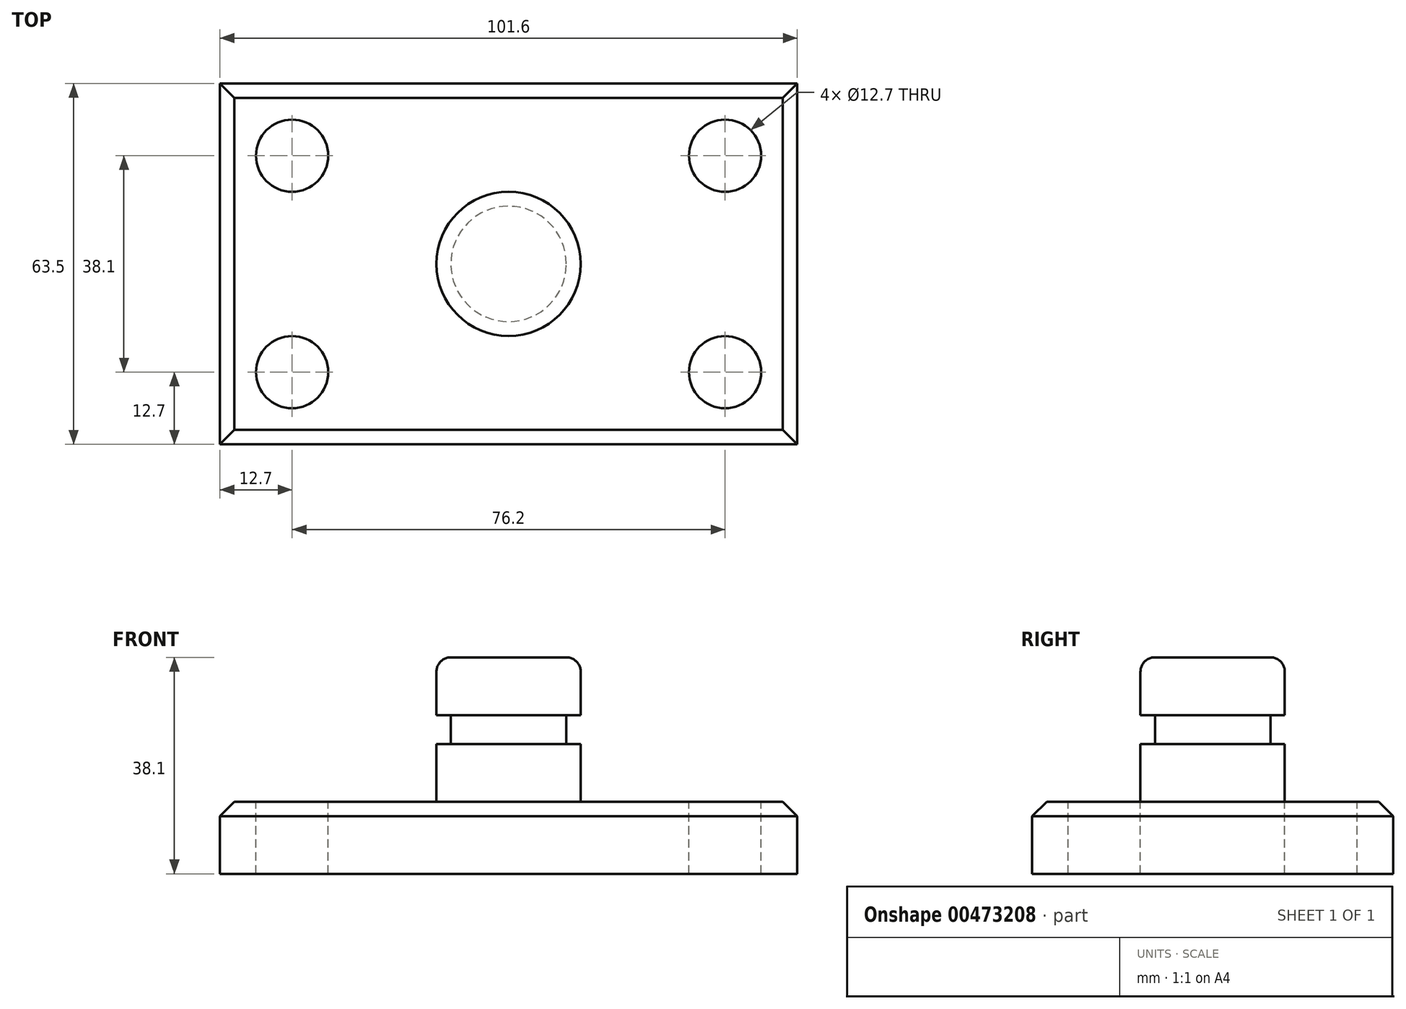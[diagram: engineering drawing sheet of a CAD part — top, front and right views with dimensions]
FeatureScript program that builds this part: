
annotation { "Feature Type Name" : "Feature", "Feature Type Description" : "" }
export const myFeature = defineFeature(function(context is Context, id is Id, definition is map)
    precondition{}
    {
        {
            var Q0;
            Q0=qCreatedBy(makeId("Top.planeOp"),FACE);
            var sketch = newSketch(context, id + "F0", { "sketchPlane" : qUnion([Q0])});
            skLineSegment(sketch, "E0.bottom", {"start": v(50.8, 31.75) * mm, "end": v(-50.8, 31.75) * mm});
            skLineSegment(sketch, "E0.top", {"start": v(50.8, -31.75) * mm, "end": v(-50.8, -31.75) * mm});
            skLineSegment(sketch, "E0.left", {"start": v(50.8, 31.75) * mm, "end": v(50.8, -31.75) * mm});
            skLineSegment(sketch, "E0.right", {"start": v(-50.8, 31.75) * mm, "end": v(-50.8, -31.75) * mm});
            skPoint(sketch, "E0.middle", {"position": v(0, 0) * mm});
            skSolve(sketch);
        }
        {
            var Q0;
            Q0=makeQuery(id+"F0.imprint","IMPRINT",FACE,{"disambiguationData":[TD([[makeQuery(id+"F0.imprint","IMPRINT",EDGE,{"derivedFrom":sQuery(id+"F0.wireOp",EDGE,"E0.bottom")}),1.0]])]});
            extrude(context, id + "F1", {"entities" : qUnion([Q0]), "depth" : 12.7 * mm});
        }
        {
            var Q0;
            Q0=makeQuery(id+"F1.opExtrude","CAP_FACE",FACE,{"disambiguationData":[OSD([sQuery(id+"F0.wireOp",EDGE,"E0.bottom"),sQuery(id+"F0.wireOp",EDGE,"E0.top"),sQuery(id+"F0.wireOp",EDGE,"E0.left"),sQuery(id+"F0.wireOp",EDGE,"E0.right")])],"isStart":false});
            var sketch = newSketch(context, id + "F2", { "sketchPlane" : qUnion([Q0])});
            skCircle(sketch, "E1", {"center": v(-38.1, 19.05) * mm, "radius": 6.35 * mm});
            skCircle(sketch, "E2", {"center": v(38.1, 19.05) * mm, "radius": 6.35 * mm});
            skCircle(sketch, "E3", {"center": v(38.1, -19.05) * mm, "radius": 6.35 * mm});
            skCircle(sketch, "E4", {"center": v(-38.1, -19.05) * mm, "radius": 6.35 * mm});
            skSolve(sketch);
        }
        {
            var Q0;
            Q0=makeQuery(id+"F2.imprint","IMPRINT",FACE,{"disambiguationData":[TD([[makeQuery(id+"F2.imprint","IMPRINT",EDGE,{"derivedFrom":sQuery(id+"F2.wireOp",EDGE,"E1")}),1.0]])]});
            var Q1;
            Q1=makeQuery(id+"F2.imprint","IMPRINT",FACE,{"disambiguationData":[TD([[makeQuery(id+"F2.imprint","IMPRINT",EDGE,{"derivedFrom":sQuery(id+"F2.wireOp",EDGE,"E4")}),1.0]])]});
            var Q2;
            Q2=makeQuery(id+"F2.imprint","IMPRINT",FACE,{"disambiguationData":[TD([[makeQuery(id+"F2.imprint","IMPRINT",EDGE,{"derivedFrom":sQuery(id+"F2.wireOp",EDGE,"E3")}),1.0]])]});
            var Q3;
            Q3=makeQuery(id+"F2.imprint","IMPRINT",FACE,{"disambiguationData":[TD([[makeQuery(id+"F2.imprint","IMPRINT",EDGE,{"derivedFrom":sQuery(id+"F2.wireOp",EDGE,"E2")}),1.0]])]});
            extrude(context, id + "F3", {"entities" : qUnion([Q0, Q1, Q2, Q3]), "operationType" : NewBodyOperationType.REMOVE, "endBound" : BoundingType.THROUGH_ALL, "oppositeDirection" : true, "depth" : 25.4 * mm});
        }
        {
            var Q0;
            Q0=qCreatedBy(makeId("Front.planeOp"),FACE);
            var sketch = newSketch(context, id + "F4", { "sketchPlane" : qUnion([Q0])});
            skLineSegment(sketch, "E5.bottom", {"start": v(0, 12.7) * mm, "end": v(12.7, 12.7) * mm});
            skLineSegment(sketch, "E5.top", {"start": v(0, 38.1) * mm, "end": v(12.7, 38.1) * mm});
            skLineSegment(sketch, "E5.left", {"start": v(0, 12.7) * mm, "end": v(0, 38.1) * mm});
            skLineSegment(sketch, "E5.right", {"start": v(12.7, 12.7) * mm, "end": v(12.7, 38.1) * mm});
            skSolve(sketch);
        }
        {
            var Q0;
            Q0=makeQuery(id+"F4.imprint","IMPRINT",FACE,{"disambiguationData":[TD([[makeQuery(id+"F4.imprint","IMPRINT",EDGE,{"derivedFrom":sQuery(id+"F4.wireOp",EDGE,"E5.bottom")}),1.0]])]});
            var Q1;
            Q1=sQuery(id+"F4.wireOp",EDGE,"E5.left");
            revolve(context, id + "F5", {"operationType" : NewBodyOperationType.ADD, "entities" : qUnion([Q0]), "axis" : qUnion([Q1]), "revolveType" : RevolveType.FULL});
        }
        {
            var Q0;
            Q0=qCreatedBy(makeId("Front.planeOp"),FACE);
            var sketch = newSketch(context, id + "F6", { "sketchPlane" : qUnion([Q0])});
            skLineSegment(sketch, "E6.bottom", {"start": v(14.97, 27.94) * mm, "end": v(10.16, 27.94) * mm});
            skLineSegment(sketch, "E6.top", {"start": v(14.97, 22.86) * mm, "end": v(10.16, 22.86) * mm});
            skLineSegment(sketch, "E6.left", {"start": v(14.97, 27.94) * mm, "end": v(14.97, 22.86) * mm});
            skLineSegment(sketch, "E6.right", {"start": v(10.16, 27.94) * mm, "end": v(10.16, 22.86) * mm});
            skSolve(sketch);
        }
        {
            var Q0;
            Q0 = qSketchRegion(id + "F6", true);
            var Q1;
            Q1=makeQuery(id+"F5.opRevolve","SWEPT_FACE",FACE,{"disambiguationData":[OSD([sQuery(id+"F4.wireOp",EDGE,"E5.right")])]});
            revolve(context, id + "F7", {"operationType" : NewBodyOperationType.REMOVE, "entities" : qUnion([Q0]), "axis" : qUnion([Q1]), "revolveType" : RevolveType.FULL, "oppositeDirection" : true});
        }
        {
            var Q0;
            Q0=makeQuery(id+"F5.opRevolve","SWEPT_EDGE",EDGE,{"disambiguationData":[OSD([sQuery(id+"F4.wireOp",EDGE,"E5.bottom"),sQuery(id+"F4.wireOp",EDGE,"E5.right")])]});
            var Q1;
            Q1=makeQuery(id+"F5.opRevolve","SWEPT_EDGE",EDGE,{"disambiguationData":[OSD([sQuery(id+"F4.wireOp",EDGE,"E5.top"),sQuery(id+"F4.wireOp",EDGE,"E5.right")])]});
            fillet(context, id + "F8", {"entities" : qUnion([Q0, Q1]), "radius" : 2.54 * mm, "tangentPropagation" : true, "allowEdgeOverflow" : false});
        }
        {
            var Q0;
            Q0=makeQuery(id+"F1.opExtrude","CAP_EDGE",EDGE,{"disambiguationData":[OSD([sQuery(id+"F0.wireOp",EDGE,"E0.top")])],"isStart":false});
            var Q1;
            Q1=makeQuery(id+"F1.opExtrude","CAP_EDGE",EDGE,{"disambiguationData":[OSD([sQuery(id+"F0.wireOp",EDGE,"E0.left")])],"isStart":false});
            var Q2;
            Q2=makeQuery(id+"F1.opExtrude","CAP_EDGE",EDGE,{"disambiguationData":[OSD([sQuery(id+"F0.wireOp",EDGE,"E0.bottom")])],"isStart":false});
            var Q3;
            Q3=makeQuery(id+"F1.opExtrude","CAP_EDGE",EDGE,{"disambiguationData":[OSD([sQuery(id+"F0.wireOp",EDGE,"E0.right")])],"isStart":false});
            chamfer(context, id + "F9", {"entities" : qUnion([Q0, Q1, Q2, Q3]), "width" : 2.54 * mm, "tangentPropagation" : true});
        }
    });
